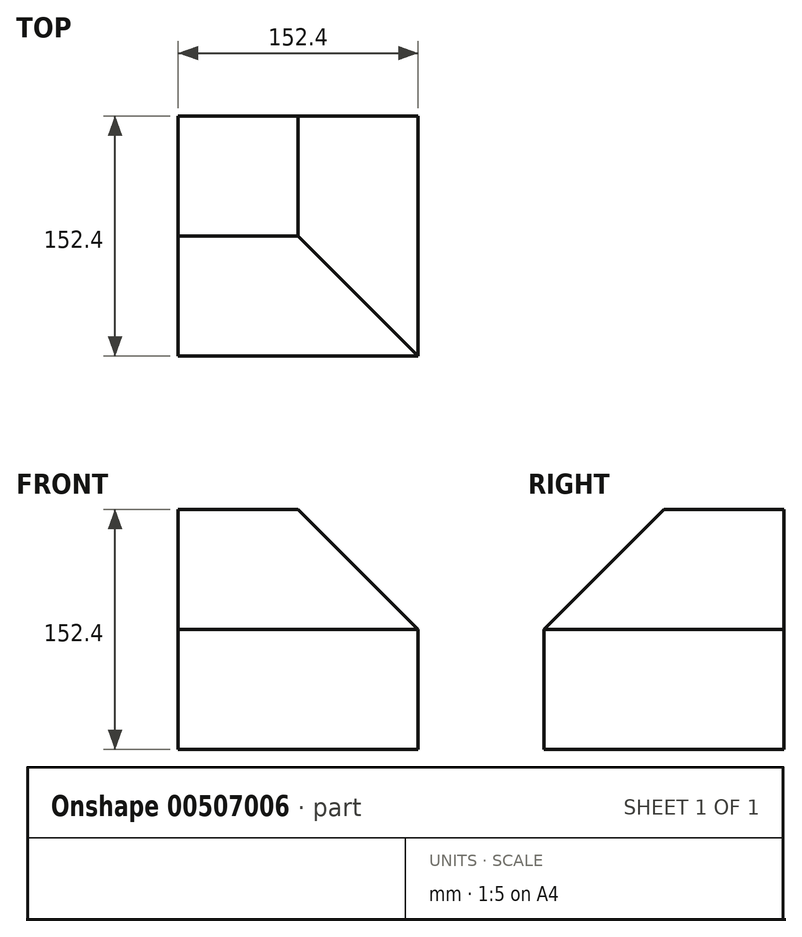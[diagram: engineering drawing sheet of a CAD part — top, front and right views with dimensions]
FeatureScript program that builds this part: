
annotation { "Feature Type Name" : "Feature", "Feature Type Description" : "" }
export const myFeature = defineFeature(function(context is Context, id is Id, definition is map)
    precondition{}
    {
        {
            var Q0;
            Q0=qCreatedBy(makeId("Top.planeOp"),FACE);
            var sketch = newSketch(context, id + "F0", { "sketchPlane" : qUnion([Q0])});
            skLineSegment(sketch, "E0.bottom", {"start": v(-76.2, 76.2) * mm, "end": v(76.2, 76.2) * mm});
            skLineSegment(sketch, "E0.top", {"start": v(-76.2, -76.2) * mm, "end": v(76.2, -76.2) * mm});
            skLineSegment(sketch, "E0.left", {"start": v(-76.2, 76.2) * mm, "end": v(-76.2, -76.2) * mm});
            skLineSegment(sketch, "E0.right", {"start": v(76.2, 76.2) * mm, "end": v(76.2, -76.2) * mm});
            skSolve(sketch);
        }
        {
            var Q0;
            Q0 = qSketchRegion(id + "F0", true);
            extrude(context, id + "F1", {"entities" : qUnion([Q0]), "endBound" : BoundingType.SYMMETRIC, "depth" : 152.4 * mm});
        }
        {
            var Q0;
            Q0=makeQuery(id+"F1.opExtrude","SWEPT_FACE",FACE,{"disambiguationData":[OSD([sQuery(id+"F0.wireOp",EDGE,"E0.right")])]});
            var sketch = newSketch(context, id + "F2", { "sketchPlane" : qUnion([Q0])});
            skLineSegment(sketch, "E1", {"start": v(-76.2, 0) * mm, "end": v(0, 76.2) * mm});
            skLineSegment(sketch, "E2", {"start": v(-76.2, 76.2) * mm, "end": v(0, 76.2) * mm});
            skLineSegment(sketch, "E3", {"start": v(-76.2, 76.2) * mm, "end": v(-76.2, 0) * mm});
            skSolve(sketch);
        }
        {
            var Q0;
            Q0=makeQuery(id+"F1.opExtrude","SWEPT_FACE",FACE,{"disambiguationData":[OSD([sQuery(id+"F0.wireOp",EDGE,"E0.top")])]});
            var sketch = newSketch(context, id + "F3", { "sketchPlane" : qUnion([Q0])});
            skLineSegment(sketch, "E4", {"start": v(0, 76.2) * mm, "end": v(76.2, 0) * mm});
            skLineSegment(sketch, "E5", {"start": v(76.2, 0) * mm, "end": v(76.2, 76.2) * mm});
            skLineSegment(sketch, "E6", {"start": v(76.2, 76.2) * mm, "end": v(0, 76.2) * mm});
            skSolve(sketch);
        }
        {
            var Q0;
            Q0 = qSketchRegion(id + "F2", true);
            extrude(context, id + "F4", {"entities" : qUnion([Q0]), "operationType" : NewBodyOperationType.REMOVE, "endBound" : BoundingType.THROUGH_ALL, "oppositeDirection" : true, "depth" : 25.4 * mm});
        }
        {
            var Q0;
            Q0 = qSketchRegion(id + "F3", true);
            extrude(context, id + "F5", {"entities" : qUnion([Q0]), "operationType" : NewBodyOperationType.REMOVE, "endBound" : BoundingType.THROUGH_ALL, "oppositeDirection" : true, "depth" : 25.4 * mm});
        }
    });
